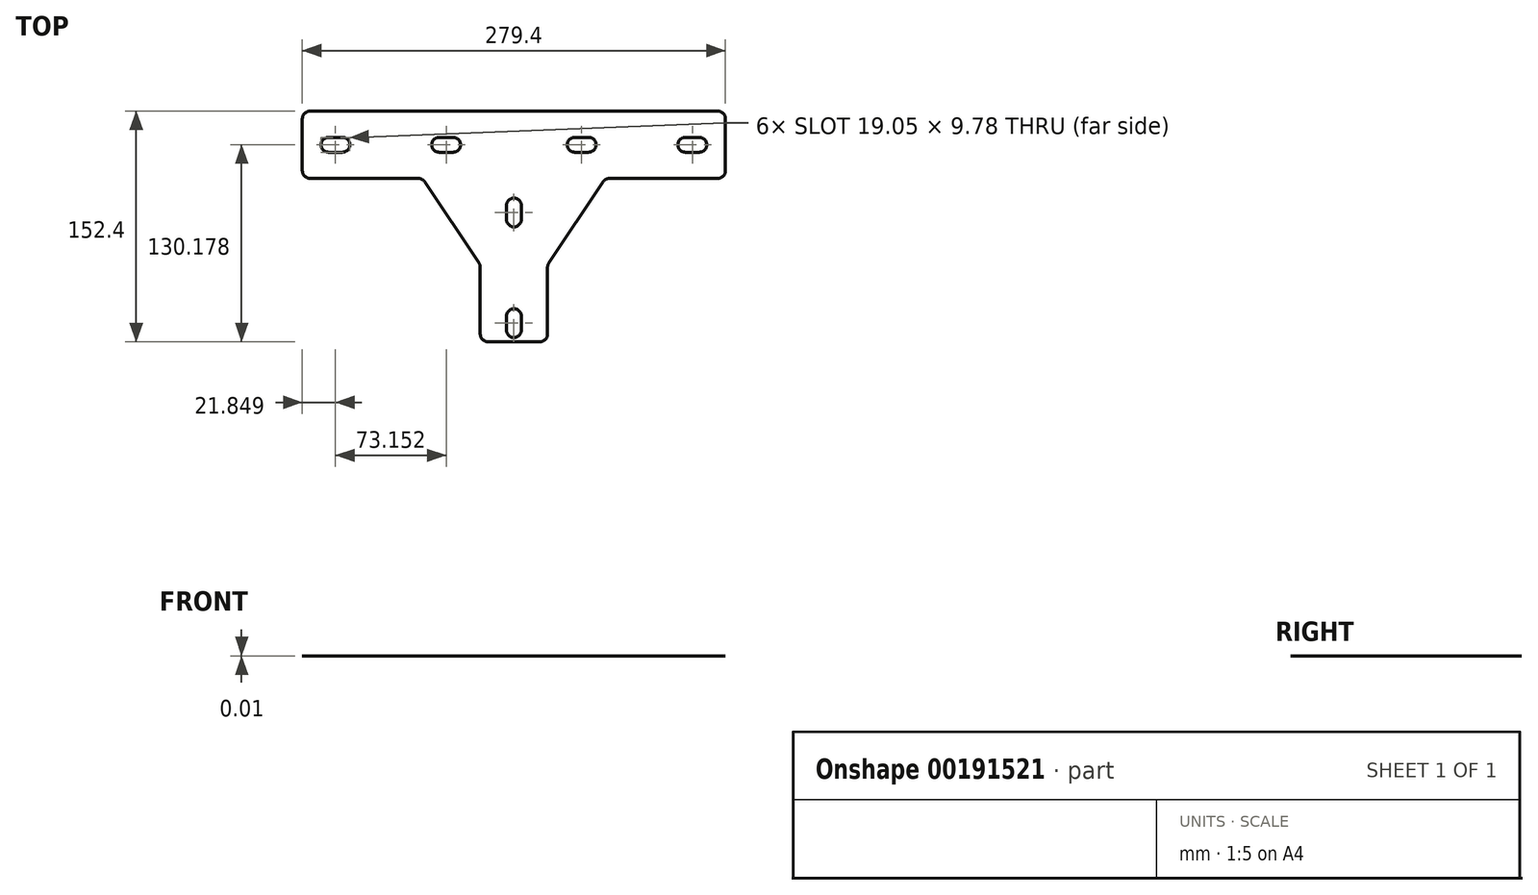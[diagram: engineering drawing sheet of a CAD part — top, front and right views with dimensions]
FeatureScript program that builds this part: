
annotation { "Feature Type Name" : "Feature", "Feature Type Description" : "" }
export const myFeature = defineFeature(function(context is Context, id is Id, definition is map)
    precondition{}
    {
        {
            var Q0;
            Q0=qCreatedBy(makeId("Top.planeOp"),FACE);
            var sketch = newSketch(context, id + "F0", { "sketchPlane" : qUnion([Q0])});
            skLineSegment(sketch, "E0", {"start": v(-155.35, 72.1) * mm, "end": v(124.05, 72.1) * mm});
            skLineSegment(sketch, "E1", {"start": v(124.05, 72.1) * mm, "end": v(124.05, 27.64) * mm});
            skLineSegment(sketch, "E2", {"start": v(124.05, 27.64) * mm, "end": v(44.7, 27.64) * mm});
            skLineSegment(sketch, "E3", {"start": v(44.7, 27.64) * mm, "end": v(6.58, -29.5) * mm});
            skLineSegment(sketch, "E4", {"start": v(6.58, -29.5) * mm, "end": v(6.58, -80.3) * mm});
            skLineSegment(sketch, "E5", {"start": v(6.58, -80.3) * mm, "end": v(-37.87, -80.3) * mm});
            skLineSegment(sketch, "E6", {"start": v(-37.87, -80.3) * mm, "end": v(-37.87, -29.5) * mm});
            skLineSegment(sketch, "E7", {"start": v(-37.87, -29.5) * mm, "end": v(-76, 27.64) * mm});
            skLineSegment(sketch, "E8", {"start": v(-76, 27.64) * mm, "end": v(-155.35, 27.64) * mm});
            skLineSegment(sketch, "E9", {"start": v(-155.35, 27.64) * mm, "end": v(-155.35, 72.1) * mm});
            skSolve(sketch);
        }
        {
            var Q0;
            Q0 = qSketchRegion(id + "F0", true);
            extrude(context, id + "F1", {"entities" : qUnion([Q0]), "depth" : 3 / 406.4 * mm});
        }
        {
            var Q0;
            Q0=makeQuery(id+"F1.opExtrude","SWEPT_EDGE",EDGE,{"disambiguationData":[OSD([sQuery(id+"F0.wireOp",EDGE,"E8"),sQuery(id+"F0.wireOp",EDGE,"E9")])]});
            var Q1;
            Q1=makeQuery(id+"F1.opExtrude","SWEPT_EDGE",EDGE,{"disambiguationData":[OSD([sQuery(id+"F0.wireOp",EDGE,"E0"),sQuery(id+"F0.wireOp",EDGE,"E9")])]});
            var Q2;
            Q2=makeQuery(id+"F1.opExtrude","SWEPT_EDGE",EDGE,{"disambiguationData":[OSD([sQuery(id+"F0.wireOp",EDGE,"E5"),sQuery(id+"F0.wireOp",EDGE,"E6")])]});
            var Q3;
            Q3=makeQuery(id+"F1.opExtrude","SWEPT_EDGE",EDGE,{"disambiguationData":[OSD([sQuery(id+"F0.wireOp",EDGE,"E4"),sQuery(id+"F0.wireOp",EDGE,"E5")])]});
            var Q4;
            Q4=makeQuery(id+"F1.opExtrude","SWEPT_EDGE",EDGE,{"disambiguationData":[OSD([sQuery(id+"F0.wireOp",EDGE,"E7"),sQuery(id+"F0.wireOp",EDGE,"E8")])]});
            var Q5;
            Q5=makeQuery(id+"F1.opExtrude","SWEPT_EDGE",EDGE,{"disambiguationData":[OSD([sQuery(id+"F0.wireOp",EDGE,"E6"),sQuery(id+"F0.wireOp",EDGE,"E7")])]});
            var Q6;
            Q6=makeQuery(id+"F1.opExtrude","SWEPT_EDGE",EDGE,{"disambiguationData":[OSD([sQuery(id+"F0.wireOp",EDGE,"E3"),sQuery(id+"F0.wireOp",EDGE,"E4")])]});
            var Q7;
            Q7=makeQuery(id+"F1.opExtrude","SWEPT_EDGE",EDGE,{"disambiguationData":[OSD([sQuery(id+"F0.wireOp",EDGE,"E2"),sQuery(id+"F0.wireOp",EDGE,"E3")])]});
            var Q8;
            Q8=makeQuery(id+"F1.opExtrude","SWEPT_EDGE",EDGE,{"disambiguationData":[OSD([sQuery(id+"F0.wireOp",EDGE,"E1"),sQuery(id+"F0.wireOp",EDGE,"E2")])]});
            var Q9;
            Q9=makeQuery(id+"F1.opExtrude","SWEPT_EDGE",EDGE,{"disambiguationData":[OSD([sQuery(id+"F0.wireOp",EDGE,"E0"),sQuery(id+"F0.wireOp",EDGE,"E1")])]});
            fillet(context, id + "F2", {"entities" : qUnion([Q0, Q1, Q2, Q3, Q4, Q5, Q6, Q7, Q8, Q9]), "radius" : 5.08 * mm, "tangentPropagation" : true, "allowEdgeOverflow" : false});
        }
        {
            var Q0;
            Q0=makeQuery(id+"F1.opExtrude","CAP_FACE",FACE,{"disambiguationData":[OSD([sQuery(id+"F0.wireOp",EDGE,"E0"),sQuery(id+"F0.wireOp",EDGE,"E1"),sQuery(id+"F0.wireOp",EDGE,"E2"),sQuery(id+"F0.wireOp",EDGE,"E3"),sQuery(id+"F0.wireOp",EDGE,"E4"),sQuery(id+"F0.wireOp",EDGE,"E5"),sQuery(id+"F0.wireOp",EDGE,"E6"),sQuery(id+"F0.wireOp",EDGE,"E7"),sQuery(id+"F0.wireOp",EDGE,"E8"),sQuery(id+"F0.wireOp",EDGE,"E9")])],"isStart":false});
            var sketch = newSketch(context, id + "F3", { "sketchPlane" : qUnion([Q0])});
            skLineSegment(sketch, "E10", {"start": v(124.05, 49.87) * mm, "end": v(-155.35, 49.87) * mm, "construction": true});
            skLineSegment(sketch, "E11", {"start": v(-15.65, -80.3) * mm, "end": v(-15.65, 49.87) * mm, "construction": true});
            skLineSegment(sketch, "E12", {"start": v(97.57, 54.76) * mm, "end": v(106.85, 54.76) * mm});
            skLineSegment(sketch, "E13", {"start": v(97.57, 44.98) * mm, "end": v(106.85, 44.98) * mm});
            skArc(sketch, "E14", {"start": v(106.85, 54.76) * mm, "mid": v(111.74, 49.87) * mm, "end": v(106.85, 44.98) * mm});
            skArc(sketch, "E15", {"start": v(97.57, 54.76) * mm, "mid": v(92.69, 49.87) * mm, "end": v(97.57, 44.98) * mm});
            skLineSegment(sketch, "E16", {"start": v(24.42, 54.76) * mm, "end": v(33.7, 54.76) * mm});
            skLineSegment(sketch, "E17", {"start": v(24.42, 44.98) * mm, "end": v(33.7, 44.98) * mm});
            skArc(sketch, "E18", {"start": v(33.7, 54.76) * mm, "mid": v(38.58, 49.87) * mm, "end": v(33.7, 44.98) * mm});
            skArc(sketch, "E19", {"start": v(24.42, 54.76) * mm, "mid": v(19.53, 49.87) * mm, "end": v(24.42, 44.98) * mm});
            skLineSegment(sketch, "E20", {"start": v(-15.65, 49.87) * mm, "end": v(53.15, -18.93) * mm, "construction": true});
            skLineSegment(sketch, "E21.MirrorCS", {"start": v(-20.54, -63.35) * mm, "end": v(-20.54, -72.62) * mm});
            skLineSegment(sketch, "E22.MirrorCS", {"start": v(-10.76, -63.35) * mm, "end": v(-10.76, -72.62) * mm});
            skArc(sketch, "E23.MirrorCS", {"start": v(-20.54, -72.62) * mm, "mid": v(-15.65, -77.51) * mm, "end": v(-10.76, -72.62) * mm});
            skArc(sketch, "E24.MirrorCS", {"start": v(-20.54, -63.35) * mm, "mid": v(-15.65, -58.46) * mm, "end": v(-10.76, -63.35) * mm});
            skLineSegment(sketch, "E25.MirrorCS", {"start": v(-10.76, 9.8) * mm, "end": v(-10.76, 0.53) * mm});
            skLineSegment(sketch, "E26.MirrorCS", {"start": v(-20.54, 9.8) * mm, "end": v(-20.54, 0.53) * mm});
            skArc(sketch, "E27.MirrorCS", {"start": v(-20.54, 0.53) * mm, "mid": v(-15.65, -4.36) * mm, "end": v(-10.76, 0.53) * mm});
            skArc(sketch, "E28.MirrorCS", {"start": v(-20.54, 9.8) * mm, "mid": v(-15.65, 14.69) * mm, "end": v(-10.76, 9.8) * mm});
            skLineSegment(sketch, "E29", {"start": v(-138.14, 54.76) * mm, "end": v(-128.87, 54.76) * mm});
            skLineSegment(sketch, "E30", {"start": v(-138.14, 44.98) * mm, "end": v(-128.87, 44.98) * mm});
            skArc(sketch, "E31", {"start": v(-128.87, 54.76) * mm, "mid": v(-123.98, 49.87) * mm, "end": v(-128.87, 44.98) * mm});
            skArc(sketch, "E32", {"start": v(-138.14, 54.76) * mm, "mid": v(-143.03, 49.87) * mm, "end": v(-138.14, 44.98) * mm});
            skLineSegment(sketch, "E33", {"start": v(-64.99, 54.76) * mm, "end": v(-55.71, 54.76) * mm});
            skLineSegment(sketch, "E34", {"start": v(-64.99, 44.98) * mm, "end": v(-55.71, 44.98) * mm});
            skArc(sketch, "E35", {"start": v(-55.71, 54.76) * mm, "mid": v(-50.82, 49.87) * mm, "end": v(-55.71, 44.98) * mm});
            skArc(sketch, "E36", {"start": v(-64.99, 54.76) * mm, "mid": v(-69.87, 49.87) * mm, "end": v(-64.99, 44.98) * mm});
            skSolve(sketch);
        }
        {
            var Q0;
            Q0 = qSketchRegion(id + "F3", true);
            extrude(context, id + "F4", {"entities" : qUnion([Q0]), "operationType" : NewBodyOperationType.REMOVE, "endBound" : BoundingType.THROUGH_ALL, "oppositeDirection" : true, "depth" : 25.4 * mm});
        }
    });
